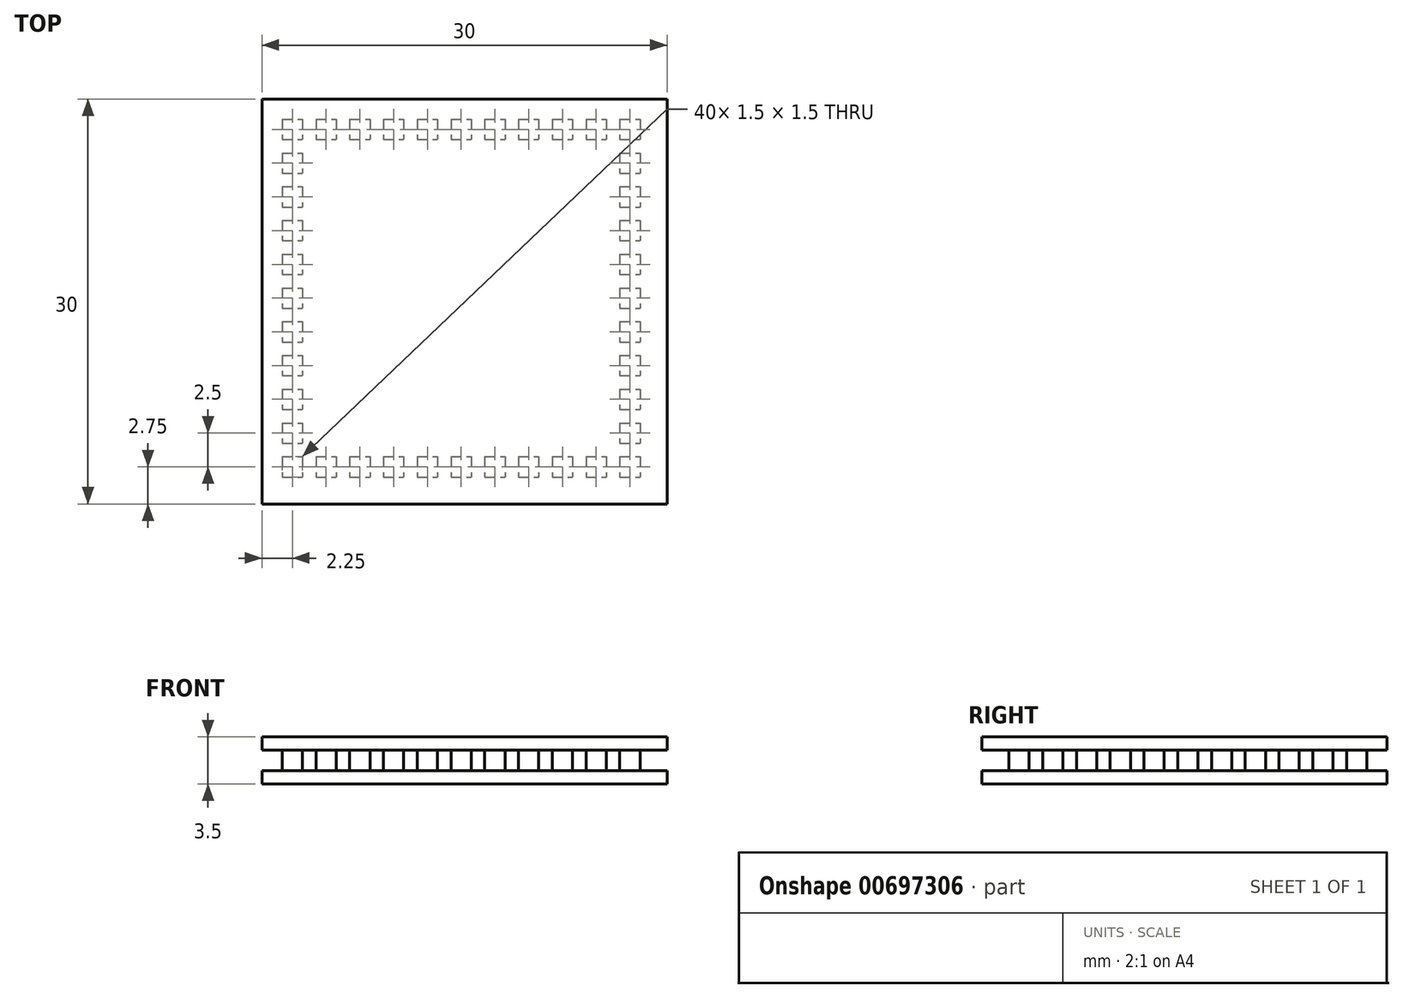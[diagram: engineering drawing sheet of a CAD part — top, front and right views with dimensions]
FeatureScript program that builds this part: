
annotation { "Feature Type Name" : "Feature", "Feature Type Description" : "" }
export const myFeature = defineFeature(function(context is Context, id is Id, definition is map)
    precondition{}
    {
        {
            var Q0;
            Q0=qCreatedBy(makeId("Top.planeOp"),FACE);
            var sketch = newSketch(context, id + "F0", { "sketchPlane" : qUnion([Q0])});
            skLineSegment(sketch, "E0.bottom", {"start": v(-15, 15) * mm, "end": v(15, 15) * mm});
            skLineSegment(sketch, "E0.top", {"start": v(-15, -15) * mm, "end": v(15, -15) * mm});
            skLineSegment(sketch, "E0.left", {"start": v(-15, 15) * mm, "end": v(-15, -15) * mm});
            skLineSegment(sketch, "E0.right", {"start": v(15, 15) * mm, "end": v(15, -15) * mm});
            skSolve(sketch);
        }
        {
            var Q0;
            Q0 = qSketchRegion(id + "F0", true);
            extrude(context, id + "F1", {"entities" : qUnion([Q0]), "oppositeDirection" : true, "depth" : 1 * mm, "offsetDistance" : 25 * mm});
        }
        {
            var Q0;
            Q0=makeQuery(id+"F1.opExtrude","CAP_FACE",FACE,{"disambiguationData":[OSD([sQuery(id+"F0.wireOp",EDGE,"E0.bottom"),sQuery(id+"F0.wireOp",EDGE,"E0.top"),sQuery(id+"F0.wireOp",EDGE,"E0.left"),sQuery(id+"F0.wireOp",EDGE,"E0.right")])],"isStart":true});
            var sketch = newSketch(context, id + "F2", { "sketchPlane" : qUnion([Q0])});
            skLineSegment(sketch, "E1.bottom", {"start": v(-13.5, 13.5) * mm, "end": v(-12, 13.5) * mm});
            skLineSegment(sketch, "E1.top", {"start": v(-13.5, 12) * mm, "end": v(-12, 12) * mm});
            skLineSegment(sketch, "E1.left", {"start": v(-13.5, 13.5) * mm, "end": v(-13.5, 12) * mm});
            skLineSegment(sketch, "E1.right", {"start": v(-12, 13.5) * mm, "end": v(-12, 12) * mm});
            skLineSegment(sketch, "E2.1.0.0", {"start": v(-11, 13.5) * mm, "end": v(-9.5, 13.5) * mm});
            skLineSegment(sketch, "E2.1.0.1", {"start": v(-11, 13.5) * mm, "end": v(-11, 12) * mm});
            skLineSegment(sketch, "E2.1.0.2", {"start": v(-11, 12) * mm, "end": v(-9.5, 12) * mm});
            skLineSegment(sketch, "E2.1.0.3", {"start": v(-9.5, 13.5) * mm, "end": v(-9.5, 12) * mm});
            skLineSegment(sketch, "E2.2.0.0", {"start": v(-8.5, 13.5) * mm, "end": v(-7, 13.5) * mm});
            skLineSegment(sketch, "E2.2.0.1", {"start": v(-8.5, 13.5) * mm, "end": v(-8.5, 12) * mm});
            skLineSegment(sketch, "E2.2.0.2", {"start": v(-8.5, 12) * mm, "end": v(-7, 12) * mm});
            skLineSegment(sketch, "E2.2.0.3", {"start": v(-7, 13.5) * mm, "end": v(-7, 12) * mm});
            skLineSegment(sketch, "E2.3.0.0", {"start": v(-6, 13.5) * mm, "end": v(-4.5, 13.5) * mm});
            skLineSegment(sketch, "E2.3.0.1", {"start": v(-6, 13.5) * mm, "end": v(-6, 12) * mm});
            skLineSegment(sketch, "E2.3.0.2", {"start": v(-6, 12) * mm, "end": v(-4.5, 12) * mm});
            skLineSegment(sketch, "E2.3.0.3", {"start": v(-4.5, 13.5) * mm, "end": v(-4.5, 12) * mm});
            skLineSegment(sketch, "E2.4.0.0", {"start": v(-3.5, 13.5) * mm, "end": v(-2, 13.5) * mm});
            skLineSegment(sketch, "E2.4.0.1", {"start": v(-3.5, 13.5) * mm, "end": v(-3.5, 12) * mm});
            skLineSegment(sketch, "E2.4.0.2", {"start": v(-3.5, 12) * mm, "end": v(-2, 12) * mm});
            skLineSegment(sketch, "E2.4.0.3", {"start": v(-2, 13.5) * mm, "end": v(-2, 12) * mm});
            skLineSegment(sketch, "E2.5.0.0", {"start": v(-1, 13.5) * mm, "end": v(0.5, 13.5) * mm});
            skLineSegment(sketch, "E2.5.0.1", {"start": v(-1, 13.5) * mm, "end": v(-1, 12) * mm});
            skLineSegment(sketch, "E2.5.0.2", {"start": v(-1, 12) * mm, "end": v(0.5, 12) * mm});
            skLineSegment(sketch, "E2.5.0.3", {"start": v(0.5, 13.5) * mm, "end": v(0.5, 12) * mm});
            skLineSegment(sketch, "E2.6.0.0", {"start": v(1.5, 13.5) * mm, "end": v(3, 13.5) * mm});
            skLineSegment(sketch, "E2.6.0.1", {"start": v(1.5, 13.5) * mm, "end": v(1.5, 12) * mm});
            skLineSegment(sketch, "E2.6.0.2", {"start": v(1.5, 12) * mm, "end": v(3, 12) * mm});
            skLineSegment(sketch, "E2.6.0.3", {"start": v(3, 13.5) * mm, "end": v(3, 12) * mm});
            skLineSegment(sketch, "E2.7.0.0", {"start": v(4, 13.5) * mm, "end": v(5.5, 13.5) * mm});
            skLineSegment(sketch, "E2.7.0.1", {"start": v(4, 13.5) * mm, "end": v(4, 12) * mm});
            skLineSegment(sketch, "E2.7.0.2", {"start": v(4, 12) * mm, "end": v(5.5, 12) * mm});
            skLineSegment(sketch, "E2.7.0.3", {"start": v(5.5, 13.5) * mm, "end": v(5.5, 12) * mm});
            skLineSegment(sketch, "E2.8.0.0", {"start": v(6.5, 13.5) * mm, "end": v(8, 13.5) * mm});
            skLineSegment(sketch, "E2.8.0.1", {"start": v(6.5, 13.5) * mm, "end": v(6.5, 12) * mm});
            skLineSegment(sketch, "E2.8.0.2", {"start": v(6.5, 12) * mm, "end": v(8, 12) * mm});
            skLineSegment(sketch, "E2.8.0.3", {"start": v(8, 13.5) * mm, "end": v(8, 12) * mm});
            skLineSegment(sketch, "E2.9.0.0", {"start": v(9, 13.5) * mm, "end": v(10.5, 13.5) * mm});
            skLineSegment(sketch, "E2.9.0.1", {"start": v(9, 13.5) * mm, "end": v(9, 12) * mm});
            skLineSegment(sketch, "E2.9.0.2", {"start": v(9, 12) * mm, "end": v(10.5, 12) * mm});
            skLineSegment(sketch, "E2.9.0.3", {"start": v(10.5, 13.5) * mm, "end": v(10.5, 12) * mm});
            skLineSegment(sketch, "E2.10.0.0", {"start": v(11.5, 13.5) * mm, "end": v(13, 13.5) * mm});
            skLineSegment(sketch, "E2.10.0.1", {"start": v(11.5, 13.5) * mm, "end": v(11.5, 12) * mm});
            skLineSegment(sketch, "E2.10.0.2", {"start": v(11.5, 12) * mm, "end": v(13, 12) * mm});
            skLineSegment(sketch, "E2.10.0.3", {"start": v(13, 13.5) * mm, "end": v(13, 12) * mm});
            skLineSegment(sketch, "E2.direction1", {"start": v(-13.5, 13.5) * mm, "end": v(-11, 13.5) * mm, "construction": true});
            skLineSegment(sketch, "E3.1.0.13", {"start": v(11.5, 9.5) * mm, "end": v(13, 9.5) * mm});
            skLineSegment(sketch, "E3.1.0.18", {"start": v(11.5, 11) * mm, "end": v(11.5, 9.5) * mm});
            skLineSegment(sketch, "E3.1.0.25", {"start": v(-12, 11) * mm, "end": v(-12, 9.5) * mm});
            skLineSegment(sketch, "E3.1.0.26", {"start": v(-13.5, 11) * mm, "end": v(-13.5, 9.5) * mm});
            skLineSegment(sketch, "E3.1.0.27", {"start": v(-13.5, 9.5) * mm, "end": v(-12, 9.5) * mm});
            skLineSegment(sketch, "E3.1.0.35", {"start": v(11.5, 11) * mm, "end": v(13, 11) * mm});
            skLineSegment(sketch, "E3.1.0.43", {"start": v(13, 11) * mm, "end": v(13, 9.5) * mm});
            skLineSegment(sketch, "E3.1.0.44", {"start": v(-13.5, 11) * mm, "end": v(-12, 11) * mm});
            skLineSegment(sketch, "E3.2.0.13", {"start": v(11.5, 7) * mm, "end": v(13, 7) * mm});
            skLineSegment(sketch, "E3.2.0.18", {"start": v(11.5, 8.5) * mm, "end": v(11.5, 7) * mm});
            skLineSegment(sketch, "E3.2.0.25", {"start": v(-12, 8.5) * mm, "end": v(-12, 7) * mm});
            skLineSegment(sketch, "E3.2.0.26", {"start": v(-13.5, 8.5) * mm, "end": v(-13.5, 7) * mm});
            skLineSegment(sketch, "E3.2.0.27", {"start": v(-13.5, 7) * mm, "end": v(-12, 7) * mm});
            skLineSegment(sketch, "E3.2.0.35", {"start": v(11.5, 8.5) * mm, "end": v(13, 8.5) * mm});
            skLineSegment(sketch, "E3.2.0.43", {"start": v(13, 8.5) * mm, "end": v(13, 7) * mm});
            skLineSegment(sketch, "E3.2.0.44", {"start": v(-13.5, 8.5) * mm, "end": v(-12, 8.5) * mm});
            skLineSegment(sketch, "E3.3.0.13", {"start": v(11.5, 4.5) * mm, "end": v(13, 4.5) * mm});
            skLineSegment(sketch, "E3.3.0.18", {"start": v(11.5, 6) * mm, "end": v(11.5, 4.5) * mm});
            skLineSegment(sketch, "E3.3.0.25", {"start": v(-12, 6) * mm, "end": v(-12, 4.5) * mm});
            skLineSegment(sketch, "E3.3.0.26", {"start": v(-13.5, 6) * mm, "end": v(-13.5, 4.5) * mm});
            skLineSegment(sketch, "E3.3.0.27", {"start": v(-13.5, 4.5) * mm, "end": v(-12, 4.5) * mm});
            skLineSegment(sketch, "E3.3.0.35", {"start": v(11.5, 6) * mm, "end": v(13, 6) * mm});
            skLineSegment(sketch, "E3.3.0.43", {"start": v(13, 6) * mm, "end": v(13, 4.5) * mm});
            skLineSegment(sketch, "E3.3.0.44", {"start": v(-13.5, 6) * mm, "end": v(-12, 6) * mm});
            skLineSegment(sketch, "E3.4.0.13", {"start": v(11.5, 2) * mm, "end": v(13, 2) * mm});
            skLineSegment(sketch, "E3.4.0.18", {"start": v(11.5, 3.5) * mm, "end": v(11.5, 2) * mm});
            skLineSegment(sketch, "E3.4.0.25", {"start": v(-12, 3.5) * mm, "end": v(-12, 2) * mm});
            skLineSegment(sketch, "E3.4.0.26", {"start": v(-13.5, 3.5) * mm, "end": v(-13.5, 2) * mm});
            skLineSegment(sketch, "E3.4.0.27", {"start": v(-13.5, 2) * mm, "end": v(-12, 2) * mm});
            skLineSegment(sketch, "E3.4.0.35", {"start": v(11.5, 3.5) * mm, "end": v(13, 3.5) * mm});
            skLineSegment(sketch, "E3.4.0.43", {"start": v(13, 3.5) * mm, "end": v(13, 2) * mm});
            skLineSegment(sketch, "E3.4.0.44", {"start": v(-13.5, 3.5) * mm, "end": v(-12, 3.5) * mm});
            skLineSegment(sketch, "E3.5.0.13", {"start": v(11.5, -0.5) * mm, "end": v(13, -0.5) * mm});
            skLineSegment(sketch, "E3.5.0.18", {"start": v(11.5, 1) * mm, "end": v(11.5, -0.5) * mm});
            skLineSegment(sketch, "E3.5.0.25", {"start": v(-12, 1) * mm, "end": v(-12, -0.5) * mm});
            skLineSegment(sketch, "E3.5.0.26", {"start": v(-13.5, 1) * mm, "end": v(-13.5, -0.5) * mm});
            skLineSegment(sketch, "E3.5.0.27", {"start": v(-13.5, -0.5) * mm, "end": v(-12, -0.5) * mm});
            skLineSegment(sketch, "E3.5.0.35", {"start": v(11.5, 1) * mm, "end": v(13, 1) * mm});
            skLineSegment(sketch, "E3.5.0.43", {"start": v(13, 1) * mm, "end": v(13, -0.5) * mm});
            skLineSegment(sketch, "E3.5.0.44", {"start": v(-13.5, 1) * mm, "end": v(-12, 1) * mm});
            skLineSegment(sketch, "E3.6.0.13", {"start": v(11.5, -3) * mm, "end": v(13, -3) * mm});
            skLineSegment(sketch, "E3.6.0.18", {"start": v(11.5, -1.5) * mm, "end": v(11.5, -3) * mm});
            skLineSegment(sketch, "E3.6.0.25", {"start": v(-12, -1.5) * mm, "end": v(-12, -3) * mm});
            skLineSegment(sketch, "E3.6.0.26", {"start": v(-13.5, -1.5) * mm, "end": v(-13.5, -3) * mm});
            skLineSegment(sketch, "E3.6.0.27", {"start": v(-13.5, -3) * mm, "end": v(-12, -3) * mm});
            skLineSegment(sketch, "E3.6.0.35", {"start": v(11.5, -1.5) * mm, "end": v(13, -1.5) * mm});
            skLineSegment(sketch, "E3.6.0.43", {"start": v(13, -1.5) * mm, "end": v(13, -3) * mm});
            skLineSegment(sketch, "E3.6.0.44", {"start": v(-13.5, -1.5) * mm, "end": v(-12, -1.5) * mm});
            skLineSegment(sketch, "E3.7.0.13", {"start": v(11.5, -5.5) * mm, "end": v(13, -5.5) * mm});
            skLineSegment(sketch, "E3.7.0.18", {"start": v(11.5, -4) * mm, "end": v(11.5, -5.5) * mm});
            skLineSegment(sketch, "E3.7.0.25", {"start": v(-12, -4) * mm, "end": v(-12, -5.5) * mm});
            skLineSegment(sketch, "E3.7.0.26", {"start": v(-13.5, -4) * mm, "end": v(-13.5, -5.5) * mm});
            skLineSegment(sketch, "E3.7.0.27", {"start": v(-13.5, -5.5) * mm, "end": v(-12, -5.5) * mm});
            skLineSegment(sketch, "E3.7.0.35", {"start": v(11.5, -4) * mm, "end": v(13, -4) * mm});
            skLineSegment(sketch, "E3.7.0.43", {"start": v(13, -4) * mm, "end": v(13, -5.5) * mm});
            skLineSegment(sketch, "E3.7.0.44", {"start": v(-13.5, -4) * mm, "end": v(-12, -4) * mm});
            skLineSegment(sketch, "E3.8.0.13", {"start": v(11.5, -8) * mm, "end": v(13, -8) * mm});
            skLineSegment(sketch, "E3.8.0.18", {"start": v(11.5, -6.5) * mm, "end": v(11.5, -8) * mm});
            skLineSegment(sketch, "E3.8.0.25", {"start": v(-12, -6.5) * mm, "end": v(-12, -8) * mm});
            skLineSegment(sketch, "E3.8.0.26", {"start": v(-13.5, -6.5) * mm, "end": v(-13.5, -8) * mm});
            skLineSegment(sketch, "E3.8.0.27", {"start": v(-13.5, -8) * mm, "end": v(-12, -8) * mm});
            skLineSegment(sketch, "E3.8.0.35", {"start": v(11.5, -6.5) * mm, "end": v(13, -6.5) * mm});
            skLineSegment(sketch, "E3.8.0.43", {"start": v(13, -6.5) * mm, "end": v(13, -8) * mm});
            skLineSegment(sketch, "E3.8.0.44", {"start": v(-13.5, -6.5) * mm, "end": v(-12, -6.5) * mm});
            skLineSegment(sketch, "E3.9.0.13", {"start": v(11.5, -10.5) * mm, "end": v(13, -10.5) * mm});
            skLineSegment(sketch, "E3.9.0.18", {"start": v(11.5, -9) * mm, "end": v(11.5, -10.5) * mm});
            skLineSegment(sketch, "E3.9.0.25", {"start": v(-12, -9) * mm, "end": v(-12, -10.5) * mm});
            skLineSegment(sketch, "E3.9.0.26", {"start": v(-13.5, -9) * mm, "end": v(-13.5, -10.5) * mm});
            skLineSegment(sketch, "E3.9.0.27", {"start": v(-13.5, -10.5) * mm, "end": v(-12, -10.5) * mm});
            skLineSegment(sketch, "E3.9.0.35", {"start": v(11.5, -9) * mm, "end": v(13, -9) * mm});
            skLineSegment(sketch, "E3.9.0.43", {"start": v(13, -9) * mm, "end": v(13, -10.5) * mm});
            skLineSegment(sketch, "E3.9.0.44", {"start": v(-13.5, -9) * mm, "end": v(-12, -9) * mm});
            skLineSegment(sketch, "E3.10.0.0", {"start": v(-1, -13) * mm, "end": v(0.5, -13) * mm});
            skLineSegment(sketch, "E3.10.0.1", {"start": v(9, -13) * mm, "end": v(10.5, -13) * mm});
            skLineSegment(sketch, "E3.10.0.2", {"start": v(-6, -11.5) * mm, "end": v(-4.5, -11.5) * mm});
            skLineSegment(sketch, "E3.10.0.3", {"start": v(-11, -13) * mm, "end": v(-9.5, -13) * mm});
            skLineSegment(sketch, "E3.10.0.4", {"start": v(-11, -11.5) * mm, "end": v(-9.5, -11.5) * mm});
            skLineSegment(sketch, "E3.10.0.5", {"start": v(-6, -13) * mm, "end": v(-4.5, -13) * mm});
            skLineSegment(sketch, "E3.10.0.6", {"start": v(4, -13) * mm, "end": v(5.5, -13) * mm});
            skLineSegment(sketch, "E3.10.0.7", {"start": v(4, -11.5) * mm, "end": v(5.5, -11.5) * mm});
            skLineSegment(sketch, "E3.10.0.8", {"start": v(-1, -11.5) * mm, "end": v(0.5, -11.5) * mm});
            skLineSegment(sketch, "E3.10.0.9", {"start": v(9, -11.5) * mm, "end": v(10.5, -11.5) * mm});
            skLineSegment(sketch, "E3.10.0.10", {"start": v(-2, -11.5) * mm, "end": v(-2, -13) * mm});
            skLineSegment(sketch, "E3.10.0.11", {"start": v(8, -11.5) * mm, "end": v(8, -13) * mm});
            skLineSegment(sketch, "E3.10.0.12", {"start": v(1.5, -13) * mm, "end": v(3, -13) * mm});
            skLineSegment(sketch, "E3.10.0.13", {"start": v(11.5, -13) * mm, "end": v(13, -13) * mm});
            skLineSegment(sketch, "E3.10.0.14", {"start": v(-3.5, -13) * mm, "end": v(-2, -13) * mm});
            skLineSegment(sketch, "E3.10.0.15", {"start": v(6.5, -13) * mm, "end": v(8, -13) * mm});
            skLineSegment(sketch, "E3.10.0.16", {"start": v(5.5, -11.5) * mm, "end": v(5.5, -13) * mm});
            skLineSegment(sketch, "E3.10.0.17", {"start": v(1.5, -11.5) * mm, "end": v(1.5, -13) * mm});
            skLineSegment(sketch, "E3.10.0.18", {"start": v(11.5, -11.5) * mm, "end": v(11.5, -13) * mm});
            skLineSegment(sketch, "E3.10.0.19", {"start": v(-7, -11.5) * mm, "end": v(-7, -13) * mm});
            skLineSegment(sketch, "E3.10.0.20", {"start": v(-8.5, -13) * mm, "end": v(-7, -13) * mm});
            skLineSegment(sketch, "E3.10.0.21", {"start": v(-8.5, -11.5) * mm, "end": v(-8.5, -13) * mm});
            skLineSegment(sketch, "E3.10.0.22", {"start": v(-8.5, -11.5) * mm, "end": v(-7, -11.5) * mm});
            skLineSegment(sketch, "E3.10.0.23", {"start": v(-9.5, -11.5) * mm, "end": v(-9.5, -13) * mm});
            skLineSegment(sketch, "E3.10.0.24", {"start": v(-11, -11.5) * mm, "end": v(-11, -13) * mm});
            skLineSegment(sketch, "E3.10.0.25", {"start": v(-12, -11.5) * mm, "end": v(-12, -13) * mm});
            skLineSegment(sketch, "E3.10.0.26", {"start": v(-13.5, -11.5) * mm, "end": v(-13.5, -13) * mm});
            skLineSegment(sketch, "E3.10.0.27", {"start": v(-13.5, -13) * mm, "end": v(-12, -13) * mm});
            skLineSegment(sketch, "E3.10.0.28", {"start": v(-4.5, -11.5) * mm, "end": v(-4.5, -13) * mm});
            skLineSegment(sketch, "E3.10.0.29", {"start": v(-6, -11.5) * mm, "end": v(-6, -13) * mm});
            skLineSegment(sketch, "E3.10.0.30", {"start": v(-3.5, -11.5) * mm, "end": v(-3.5, -13) * mm});
            skLineSegment(sketch, "E3.10.0.31", {"start": v(6.5, -11.5) * mm, "end": v(6.5, -13) * mm});
            skLineSegment(sketch, "E3.10.0.32", {"start": v(-1, -11.5) * mm, "end": v(-1, -13) * mm});
            skLineSegment(sketch, "E3.10.0.33", {"start": v(9, -11.5) * mm, "end": v(9, -13) * mm});
            skLineSegment(sketch, "E3.10.0.34", {"start": v(1.5, -11.5) * mm, "end": v(3, -11.5) * mm});
            skLineSegment(sketch, "E3.10.0.35", {"start": v(11.5, -11.5) * mm, "end": v(13, -11.5) * mm});
            skLineSegment(sketch, "E3.10.0.37", {"start": v(-3.5, -11.5) * mm, "end": v(-2, -11.5) * mm});
            skLineSegment(sketch, "E3.10.0.38", {"start": v(6.5, -11.5) * mm, "end": v(8, -11.5) * mm});
            skLineSegment(sketch, "E3.10.0.39", {"start": v(4, -11.5) * mm, "end": v(4, -13) * mm});
            skLineSegment(sketch, "E3.10.0.40", {"start": v(0.5, -11.5) * mm, "end": v(0.5, -13) * mm});
            skLineSegment(sketch, "E3.10.0.41", {"start": v(10.5, -11.5) * mm, "end": v(10.5, -13) * mm});
            skLineSegment(sketch, "E3.10.0.42", {"start": v(3, -11.5) * mm, "end": v(3, -13) * mm});
            skLineSegment(sketch, "E3.10.0.43", {"start": v(13, -11.5) * mm, "end": v(13, -13) * mm});
            skLineSegment(sketch, "E3.10.0.44", {"start": v(-13.5, -11.5) * mm, "end": v(-12, -11.5) * mm});
            skLineSegment(sketch, "E3.direction1", {"start": v(-13.5, 12) * mm, "end": v(-13.5, 9.5) * mm, "construction": true});
            skSolve(sketch);
        }
        {
            var Q0;
            Q0 = qSketchRegion(id + "F2", true);
            extrude(context, id + "F3", {"entities" : qUnion([Q0]), "operationType" : NewBodyOperationType.ADD, "depth" : 1.5 * mm, "offsetDistance" : 25 * mm});
        }
        {
            var Q0;
            Q0=makeQuery(id+"F3.opExtrude","CAP_FACE",FACE,{"disambiguationData":[OSD([sQuery(id+"F2.wireOp",EDGE,"E3.5.0.25"),sQuery(id+"F2.wireOp",EDGE,"E3.5.0.26"),sQuery(id+"F2.wireOp",EDGE,"E3.5.0.27"),sQuery(id+"F2.wireOp",EDGE,"E3.5.0.44")])],"isStart":false});
            var sketch = newSketch(context, id + "F4", { "sketchPlane" : qUnion([Q0])});
            skLineSegment(sketch, "E4.bottom", {"start": v(-15, 15) * mm, "end": v(15, 15) * mm});
            skLineSegment(sketch, "E4.top", {"start": v(-15, -15) * mm, "end": v(15, -15) * mm});
            skLineSegment(sketch, "E4.left", {"start": v(-15, 15) * mm, "end": v(-15, -15) * mm});
            skLineSegment(sketch, "E4.right", {"start": v(15, 15) * mm, "end": v(15, -15) * mm});
            skSolve(sketch);
        }
        {
            var Q0;
            Q0 = qSketchRegion(id + "F4", true);
            extrude(context, id + "F5", {"entities" : qUnion([Q0]), "operationType" : NewBodyOperationType.ADD, "depth" : 1 * mm, "offsetDistance" : 25 * mm});
        }
    });
